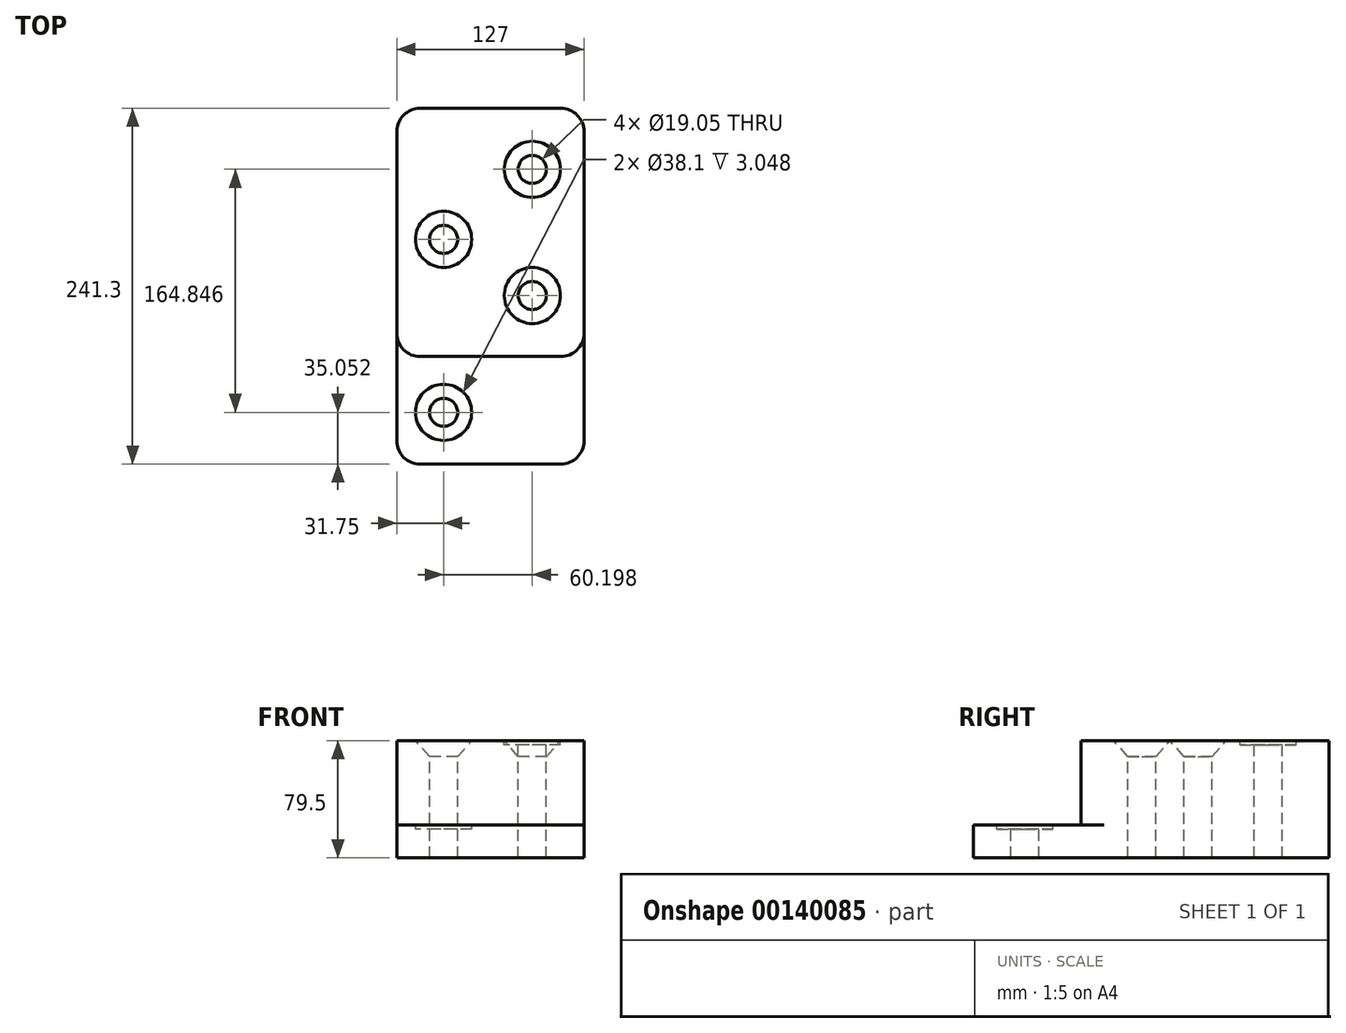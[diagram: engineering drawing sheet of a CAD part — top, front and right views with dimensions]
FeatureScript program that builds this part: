
annotation { "Feature Type Name" : "Feature", "Feature Type Description" : "" }
export const myFeature = defineFeature(function(context is Context, id is Id, definition is map)
    precondition{}
    {
        {
            var Q0;
            Q0=qCreatedBy(makeId("Top.planeOp"),FACE);
            var sketch = newSketch(context, id + "F0", { "sketchPlane" : qUnion([Q0])});
            skLineSegment(sketch, "E0", {"start": v(-63.5, 0) * mm, "end": v(0, 0) * mm});
            skLineSegment(sketch, "E1", {"start": v(0, 0) * mm, "end": v(63.5, 0) * mm});
            skLineSegment(sketch, "E2", {"start": v(63.5, 0) * mm, "end": v(63.5, 72.9) * mm});
            skLineSegment(sketch, "E3", {"start": v(63.5, 72.9) * mm, "end": v(63.5, 241.3) * mm});
            skLineSegment(sketch, "E4", {"start": v(63.5, 241.3) * mm, "end": v(-63.5, 241.3) * mm});
            skLineSegment(sketch, "E5", {"start": v(-63.5, 241.3) * mm, "end": v(-63.5, 72.9) * mm});
            skLineSegment(sketch, "E6", {"start": v(-63.5, 72.9) * mm, "end": v(-63.5, 0) * mm});
            skLineSegment(sketch, "E7", {"start": v(-63.5, 72.9) * mm, "end": v(63.5, 72.9) * mm});
            skSolve(sketch);
        }
        {
            var Q0;
            Q0=makeQuery(id+"F0.imprint","IMPRINT",FACE,{"disambiguationData":[TD([[makeQuery(id+"F0.imprint","IMPRINT",EDGE,{"derivedFrom":sQuery(id+"F0.wireOp",EDGE,"E3")}),1.0]])]});
            extrude(context, id + "F1", {"entities" : qUnion([Q0]), "depth" : 79.5 * mm});
        }
        {
            var Q0;
            Q0=makeQuery(id+"F0.imprint","IMPRINT",FACE,{"disambiguationData":[TD([[makeQuery(id+"F0.imprint","IMPRINT",EDGE,{"derivedFrom":sQuery(id+"F0.wireOp",EDGE,"E0")}),1.0]])]});
            extrude(context, id + "F2", {"entities" : qUnion([Q0]), "operationType" : NewBodyOperationType.ADD, "depth" : 22.35 * mm});
        }
        {
            var Q0;
            Q0=makeQuery(id+"F2.opExtrude","CAP_FACE",FACE,{"disambiguationData":[OSD([sQuery(id+"F0.wireOp",EDGE,"E0"),sQuery(id+"F0.wireOp",EDGE,"E1"),sQuery(id+"F0.wireOp",EDGE,"E2"),sQuery(id+"F0.wireOp",EDGE,"E6"),sQuery(id+"F0.wireOp",EDGE,"E7")])],"isStart":false});
            var sketch = newSketch(context, id + "F3", { "sketchPlane" : qUnion([Q0])});
            skLineSegment(sketch, "E8", {"start": v(63.5, 0) * mm, "end": v(-31.75, 0) * mm, "construction": true});
            skLineSegment(sketch, "E9", {"start": v(-31.75, 0) * mm, "end": v(-31.75, 35.05) * mm, "construction": true});
            skSolve(sketch);
        }
        {
            var Q0;
            Q0=makeQuery(id+"F1.opExtrude","CAP_FACE",FACE,{"disambiguationData":[OSD([sQuery(id+"F0.wireOp",EDGE,"E3"),sQuery(id+"F0.wireOp",EDGE,"E4"),sQuery(id+"F0.wireOp",EDGE,"E5"),sQuery(id+"F0.wireOp",EDGE,"E7")])],"isStart":false});
            var sketch = newSketch(context, id + "F4", { "sketchPlane" : qUnion([Q0])});
            skLineSegment(sketch, "E10", {"start": v(63.5, 241.3) * mm, "end": v(28.45, 241.3) * mm, "construction": true});
            skLineSegment(sketch, "E11", {"start": v(28.45, 241.3) * mm, "end": v(28.45, 199.9) * mm, "construction": true});
            skLineSegment(sketch, "E12", {"start": v(28.45, 199.9) * mm, "end": v(28.45, 114.3) * mm, "construction": true});
            skLineSegment(sketch, "E13", {"start": v(28.45, 241.3) * mm, "end": v(-31.75, 241.3) * mm, "construction": true});
            skLineSegment(sketch, "E14", {"start": v(-31.75, 241.3) * mm, "end": v(-31.75, 152.4) * mm, "construction": true});
            skSolve(sketch);
        }
        {
            var Q0;
            Q0=sQuery(id+"F3.wireOp",VERTEX,"E9.end");
            var Q1;
            Q1=makeQuery(id+"F1.opExtrude","SWEPT_BODY",BODY,{"disambiguationData":[OSD([sQuery(id+"F0.wireOp",EDGE,"E3"),sQuery(id+"F0.wireOp",EDGE,"E4"),sQuery(id+"F0.wireOp",EDGE,"E5"),sQuery(id+"F0.wireOp",EDGE,"E7")])]});
            hole(context, id + "F5", {"style" : HoleStyle.C_BORE, "endStyle" : HoleEndStyle.THROUGH, "holeDiameter" : 19.05 * mm, "cBoreDiameter" : 38.1 * mm, "cBoreDepth" : 3.05 * mm, "locations" : qUnion([Q0]), "scope" : qUnion([Q1]), "isTappedThrough" : true});
        }
        {
            var Q0;
            Q0=sQuery(id+"F4.wireOp",VERTEX,"E14.end");
            var Q1;
            Q1=sQuery(id+"F4.wireOp",VERTEX,"E12.end");
            var Q2;
            Q2=makeQuery(id+"F1.opExtrude","SWEPT_BODY",BODY,{"disambiguationData":[OSD([sQuery(id+"F0.wireOp",EDGE,"E3"),sQuery(id+"F0.wireOp",EDGE,"E4"),sQuery(id+"F0.wireOp",EDGE,"E5"),sQuery(id+"F0.wireOp",EDGE,"E7")])]});
            hole(context, id + "F6", {"style" : HoleStyle.C_SINK, "endStyle" : HoleEndStyle.THROUGH, "holeDiameter" : 19.05 * mm, "cSinkDiameter" : 38.1 * mm, "cSinkAngle" : 82 * degree, "locations" : qUnion([Q0, Q1]), "scope" : qUnion([Q2]), "isTappedThrough" : true});
        }
        {
            var Q0;
            Q0=sQuery(id+"F4.wireOp",VERTEX,"E12.start");
            var Q1;
            Q1=makeQuery(id+"F1.opExtrude","SWEPT_BODY",BODY,{"disambiguationData":[OSD([sQuery(id+"F0.wireOp",EDGE,"E3"),sQuery(id+"F0.wireOp",EDGE,"E4"),sQuery(id+"F0.wireOp",EDGE,"E5"),sQuery(id+"F0.wireOp",EDGE,"E7")])]});
            hole(context, id + "F7", {"style" : HoleStyle.C_BORE, "endStyle" : HoleEndStyle.THROUGH, "holeDiameter" : 19.05 * mm, "cBoreDiameter" : 38.1 * mm, "cBoreDepth" : 3.05 * mm, "locations" : qUnion([Q0]), "scope" : qUnion([Q1]), "isTappedThrough" : true});
        }
        {
            var Q0;
            Q0=makeQuery(id+"F1.opExtrude","SWEPT_EDGE",EDGE,{"disambiguationData":[OSD([sQuery(id+"F0.wireOp",EDGE,"E2"),sQuery(id+"F0.wireOp",EDGE,"E3"),sQuery(id+"F0.wireOp",EDGE,"E7")])]});
            var Q1;
            Q1=makeQuery(id+"F1.opExtrude","SWEPT_EDGE",EDGE,{"disambiguationData":[OSD([sQuery(id+"F0.wireOp",EDGE,"E5"),sQuery(id+"F0.wireOp",EDGE,"E6"),sQuery(id+"F0.wireOp",EDGE,"E7")])]});
            var Q2;
            Q2=makeQuery(id+"F2.opExtrude","SWEPT_EDGE",EDGE,{"disambiguationData":[OSD([sQuery(id+"F0.wireOp",EDGE,"E1"),sQuery(id+"F0.wireOp",EDGE,"E2")])]});
            var Q3;
            Q3=makeQuery(id+"F2.opExtrude","SWEPT_EDGE",EDGE,{"disambiguationData":[OSD([sQuery(id+"F0.wireOp",EDGE,"E0"),sQuery(id+"F0.wireOp",EDGE,"E6")])]});
            var Q4;
            Q4=makeQuery(id+"F1.opExtrude","SWEPT_EDGE",EDGE,{"disambiguationData":[OSD([sQuery(id+"F0.wireOp",EDGE,"E3"),sQuery(id+"F0.wireOp",EDGE,"E4")])]});
            var Q5;
            Q5=makeQuery(id+"F1.opExtrude","SWEPT_EDGE",EDGE,{"disambiguationData":[OSD([sQuery(id+"F0.wireOp",EDGE,"E4"),sQuery(id+"F0.wireOp",EDGE,"E5")])]});
            fillet(context, id + "F8", {"entities" : qUnion([Q0, Q1, Q2, Q3, Q4, Q5]), "radius" : 15.75 * mm, "tangentPropagation" : true, "allowEdgeOverflow" : false});
        }
    });
